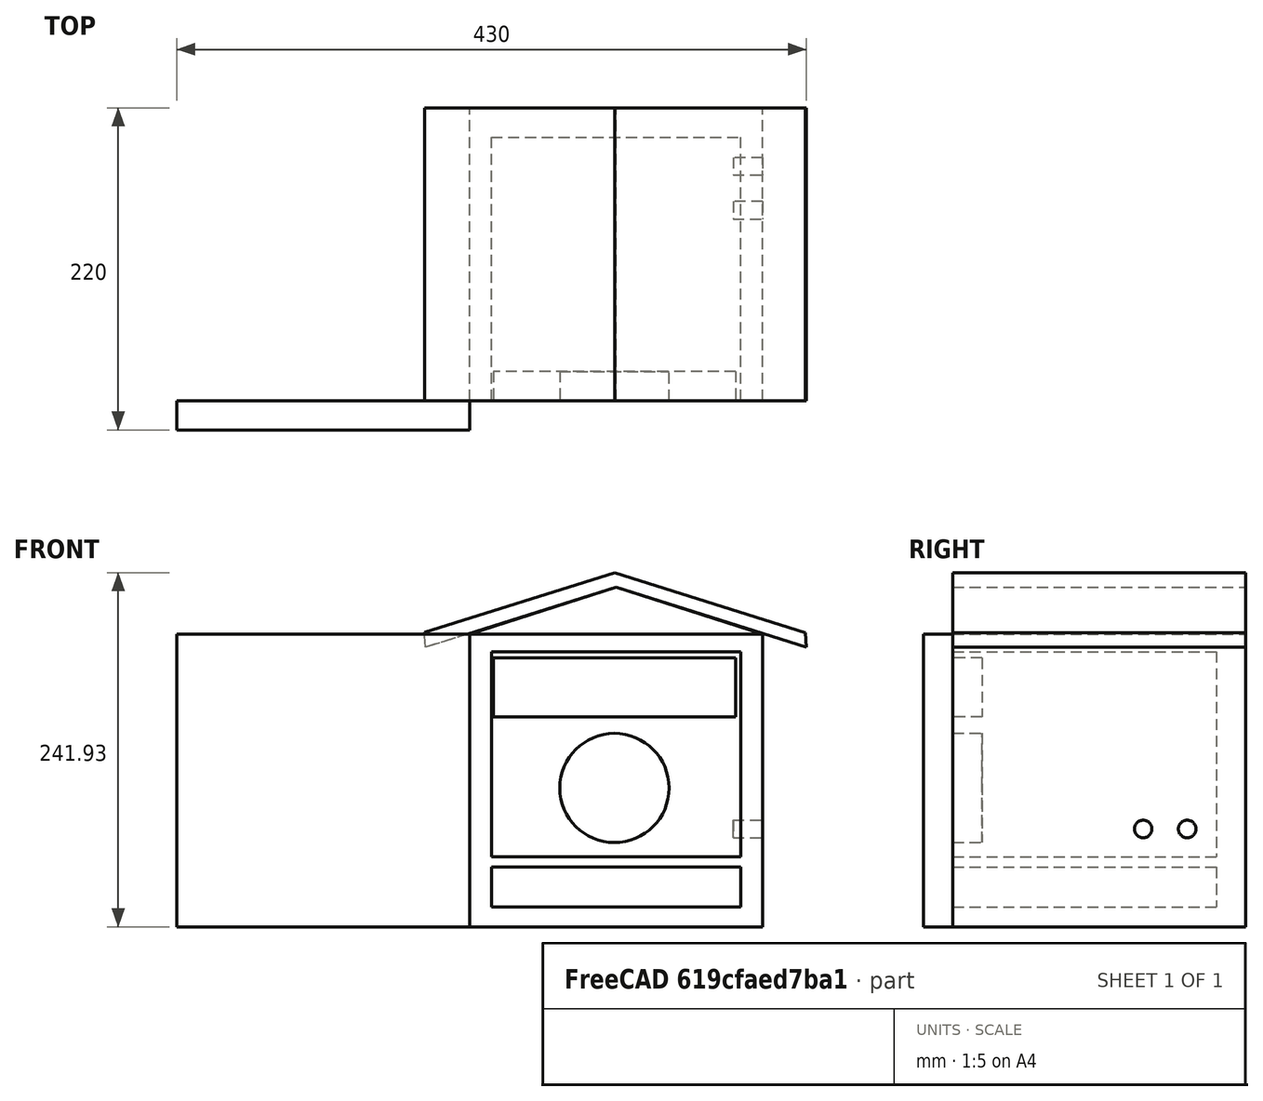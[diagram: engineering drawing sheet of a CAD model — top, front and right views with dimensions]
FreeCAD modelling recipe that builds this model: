
FCSTD DOCUMENT  (FreeCAD 0.16R6712 (Git))
Label: DSLR_Enclosure02
License: All rights reserved
LicenseURL: http://en.wikipedia.org/wiki/All_rights_reserved
objects: Drawing::FeatureViewPython×15, Drawing::FeatureViewPart×6, Sketcher::SketchObject×4, PartDesign::Pocket×3, Part::Box×2, PartDesign::Pad×1, Drawing::FeaturePage×1
note: 14 computed .brp shape members not serialized (recipe doc carries the construction recipe); baked Part::Feature solids carry a one-line shape summary decoded from their .brp

FEATURE [Part::Box] Box  label="Cube"
  Height = 200
  Length = 200
  Width = 200
FEATURE [Sketcher::SketchObject] Sketch
  Placement = pos=(0,0,0) rot=(1,0,0;1.5708rad)
  Support = -> Box [Face3]
  sketch-geometry (8):
    g0: LineSegment StartX=14.8295 StartY=187.945 StartZ=0 EndX=185.145 EndY=187.945 EndZ=0
    g1: LineSegment StartX=185.145 StartY=187.945 StartZ=0 EndX=185.145 EndY=47.8242 EndZ=0
    g2: LineSegment StartX=185.145 StartY=47.8242 StartZ=0 EndX=14.8295 EndY=47.8242 EndZ=0
    g3: LineSegment StartX=14.8295 StartY=47.8242 StartZ=0 EndX=14.8295 EndY=187.945 EndZ=0
    g4: LineSegment StartX=14.8558 StartY=40.8645 StartZ=0 EndX=185.13 EndY=40.8645 EndZ=0
    g5: LineSegment StartX=185.13 StartY=40.8645 StartZ=0 EndX=185.13 EndY=13.4597 EndZ=0
    g6: LineSegment StartX=185.13 StartY=13.4597 StartZ=0 EndX=14.8558 EndY=13.4597 EndZ=0
    g7: LineSegment StartX=14.8558 StartY=13.4597 StartZ=0 EndX=14.8558 EndY=40.8645 EndZ=0
  constraints (16):
    c: Coincident(g0,g1)
    c: Coincident(g1,g2)
    c: Coincident(g2,g3)
    c: Coincident(g3,g0)
    c: Horizontal(g0)
    c: Horizontal(g2)
    c: Vertical(g1)
    c: Vertical(g3)
    c: Coincident(g4,g5)
    c: Coincident(g5,g6)
    c: Coincident(g6,g7)
    c: Coincident(g7,g4)
    c: Horizontal(g4)
    c: Horizontal(g6)
    c: Vertical(g5)
    c: Vertical(g7)
FEATURE [Sketcher::SketchObject] Sketch002
  Placement = pos=(0,0,0) rot=(1,0,0;1.5708rad)
  sketch-geometry (9):
    g0: LineSegment StartX=100.011 StartY=231.935 StartZ=0 EndX=-30 EndY=191.024 EndZ=0
    g1: LineSegment StartX=-30 StartY=191.024 StartZ=0 EndX=-30.8025 EndY=201.024 EndZ=0
    g2: LineSegment StartX=-30.8025 StartY=201.024 StartZ=0 EndX=99.2083 EndY=241.935 EndZ=0
    g3: LineSegment StartX=99.2083 StartY=241.935 StartZ=0 EndX=229.197 EndY=200.955 EndZ=0
    g4: LineSegment StartX=229.197 StartY=200.955 StartZ=0 EndX=230 EndY=190.955 EndZ=0
    g5: LineSegment StartX=230 StartY=190.955 StartZ=0 EndX=100.011 EndY=231.935 EndZ=0
    g6: LineSegment StartX=100.011 StartY=231.935 StartZ=0 EndX=200.172 EndY=199.975 EndZ=0
    g7: LineSegment StartX=200.172 StartY=199.975 StartZ=0 EndX=0.002512 EndY=199.975 EndZ=0
    g8: LineSegment StartX=0.002512 StartY=199.975 StartZ=0 EndX=100.011 EndY=231.935 EndZ=0
  constraints (19):
    c: Coincident(g0,g1)
    c: Coincident(g1,g2)
    c: Coincident(g2,g3)
    c: Coincident(g3,g4)
    c: Coincident(g4,g5)
    c: Coincident(g5,g0)
    c: Equal(g2,g3)
    c: Equal(g0,g5)
    c: Equal(g4,g1)
    c: Parallel(g2,g0)
    c: Parallel(g3,g5)
    c: DistanceX(g0,g4) = 260
    c: DistanceY(g0,g1) = 10
    c: DistanceX(g0,g-1) = 30
    c: Coincident(g0,g6)
    c: Coincident(g6,g7)
    c: Horizontal(g7)
    c: Coincident(g7,g8)
    c: Coincident(g8,g6)
FEATURE [PartDesign::Pad] Pad
  Length = 200
  Length2 = 100
  Placement = pos=(0,0,0) rot=(1,0,0;1.5708rad)
  Reversed = true
  Sketch = -> Sketch002
  Type = 0
FEATURE [Part::Box] Box001  label="Cube001"
  Height = 200
  Length = 200
  Placement = pos=(0,0,0) rot=(0,0,1;3.14159rad)
  Width = 20
FEATURE [Sketcher::SketchObject] Sketch004
  Placement = pos=(0,-20,0) rot=(1,0,0;1.5708rad)
  Support = -> Box001 [Face4]
  sketch-geometry (5):
    g0: LineSegment StartX=-181.686 StartY=183.611 StartZ=0 EndX=-16.1366 EndY=183.611 EndZ=0
    g1: LineSegment StartX=-16.1366 StartY=183.611 StartZ=0 EndX=-16.1366 EndY=143.38 EndZ=0
    g2: LineSegment StartX=-16.1366 StartY=143.38 StartZ=0 EndX=-181.686 EndY=143.38 EndZ=0
    g3: LineSegment StartX=-181.686 StartY=143.38 StartZ=0 EndX=-181.686 EndY=183.611 EndZ=0
    g4: Circle CenterX=-98.9114 CenterY=94.8249 CenterZ=0 NormalX=0 NormalY=0 NormalZ=1 Radius=37.2966
  constraints (8):
    c: Coincident(g0,g1)
    c: Coincident(g1,g2)
    c: Coincident(g2,g3)
    c: Coincident(g3,g0)
    c: Horizontal(g0)
    c: Horizontal(g2)
    c: Vertical(g1)
    c: Vertical(g3)
FEATURE [PartDesign::Pocket] Pocket003
  Length = 20
  Placement = pos=(0,0,0) rot=(0,0,1;3.14159rad)
  Sketch = -> Sketch004
  Type = 0
FEATURE [Drawing::FeatureViewPart] Ortho  label="RightSide"
  Direction = (1,0,0)
  HiddenWidth = 0.15
  LineWidth = 0.35
  Rotation = -90
  Scale = 0.25
  ShowHiddenLines = false
  ShowSmoothLines = false
  Tolerance = 0.05
  ViewResult = <g id="RightSide"\n   transform="rotate(-90,165,150) translate(165,150) scale(0.25,0.25)"\n  >\n<g   stroke="rgb(0, 0, 0)"\n   stroke-width="1.4"\n   stroke-linecap="butt"\n   stroke-linejoin="miter"\n   fill="none"\n   transform="scale(1,-1)"\n  >\n<path id= "1" d=" M 0 0 L 199.975 0 " />\n<path id= "2" d=" M 0 -200 L 190.955 -200 " />\n<path id= "3" d=" M 0 0 L 0 -200 " />\n<circle cx ="66.8362" cy ="-160.008" r ="6" /><circle cx ="66.8362" cy ="-130.008" r ="6" /><path id= "6" d=" M 231.935 -1.545e-013 L 199.975 -1.3321e-013 " />\n<path id= "7" d=" M 190.955 -1.27202e-013 L 190.955 -200 " />\n<path id= "8" d=" M 200.955 -1.33863e-013 L 200.955 -200 " />\n<path id= "9" d=" M 200.955 -1.33863e-013 L 190.955 -1.27202e-013 " />\n<path id= "10" d=" M 200.955 -200 L 190.955 -200 " />\n<path id= "11" d=" M 231.935 -1.545e-013 L 199.975 -1.3321e-013 " />\n<path id= "12" d=" M 241.935 -1.61161e-013 L 200.955 -1.33863e-013 " />\n<path id= "13" d=" M 241.935 -200 L 200.955 -200 " />\n<path id= "14" d=" M 241.935 -1.61161e-013 L 241.935 -200 " />\n</g>\n</g>
  Visible = true
  X = 165
  Y = 150
FEATURE [Drawing::FeatureViewPart] Ortho001  label="TopView"
  Direction = (0,0,1)
  HiddenWidth = 0.15
  LineWidth = 0.35
  Rotation = 90
  Scale = 0.25
  ShowHiddenLines = false
  ShowSmoothLines = false
  Tolerance = 0.05
  ViewResult = <g id="TopView"\n   transform="rotate(90,30,110) translate(30,110) scale(0.25,0.25)"\n  >\n<g   stroke="rgb(0, 0, 0)"\n   stroke-width="1.4"\n   stroke-linecap="butt"\n   stroke-linejoin="miter"\n   fill="none"\n   transform="scale(1,-1)"\n  >\n<path id= "1" d=" M 0 0 L 0.0817739 0 " />\n<path id= "2" d=" M 185.274 1.04694e-014 L 14.4488 1.04694e-014 " />\n<path id= "3" d=" M 184.724 3.01073e-015 L 14.7262 3.01073e-015 " />\n<path id= "4" d=" M 0.0817739 1.33227e-013 L 100.011 1.545e-013 " />\n<path id= "5" d=" M 0.0817739 200 L 99.2083 200 " />\n<path id= "6" d=" M 100.011 1.545e-013 L 200.172 1.3321e-013 " />\n<path id= "7" d=" M 230 1.27202e-013 L 230 200 " />\n<path id= "8" d=" M 229.197 1.33863e-013 L 229.197 200 " />\n<path id= "9" d=" M 229.197 1.33863e-013 L 230 1.27202e-013 " />\n<path id= "10" d=" M 229.197 200 L 230 200 " />\n<path id= "11" d=" M -30.8025 1.33909e-013 L 99.2083 1.61161e-013 " />\n<path id= "12" d=" M 99.2083 1.61161e-013 L 229.197 1.33863e-013 " />\n<path id= "13" d=" M -30.8025 200 L 99.2083 200 " />\n<path id= "14" d=" M 99.2083 200 L 229.197 200 " />\n<path id= "15" d=" M 99.2083 1.61161e-013 L 99.2083 200 " />\n<path id= "16" d=" M -30.8025 1.33909e-013 L -30.8025 200 " />\n</g>\n</g>
  Visible = true
  X = 30
  Y = 110
FEATURE [Drawing::FeatureViewPart] Ortho002  label="BackView"
  Direction = (0,1,0)
  HiddenWidth = 0.15
  LineWidth = 0.35
  Rotation = -90
  Scale = 0.25
  ShowHiddenLines = false
  ShowSmoothLines = false
  Tolerance = 0.05
  ViewResult = <g id="BackView"\n   transform="rotate(-90,150,150) translate(150,150) scale(0.25,0.25)"\n  >\n<g   stroke="rgb(0, 0, 0)"\n   stroke-width="1.4"\n   stroke-linecap="butt"\n   stroke-linejoin="miter"\n   fill="none"\n   transform="scale(1,-1)"\n  >\n<path id= "1" d=" M 0 0 L 200 0 " />\n<path id= "2" d=" M 200 0 L 200 0.0817739 " />\n<path id= "3" d=" M 0 200 L 199.975 200 " />\n<path id= "4" d=" M 199.975 200 L 199.975 0.002512 " />\n<path id= "5" d=" M 199.975 0.002512 L 200 0.0817739 " />\n<path id= "6" d=" M 0 0 L 0 200 " />\n<path id= "7" d=" M 200 0.0817739 L 231.935 100.011 " />\n<path id= "8" d=" M 199.975 200 L 200 200 " />\n<path id= "9" d=" M 200 0.0817739 L 200 200 " />\n<path id= "10" d=" M 199.975 200.172 L 199.975 200 " />\n<path id= "11" d=" M 231.935 100.011 L 199.975 200.172 " />\n<path id= "12" d=" M 190.955 230 L 231.935 100.011 " />\n<path id= "13" d=" M 200.955 229.197 L 190.955 230 " />\n<path id= "14" d=" M 231.935 100.011 L 191.024 -30 " />\n<path id= "15" d=" M 191.024 -30 L 201.024 -30.8025 " />\n<path id= "16" d=" M 201.024 -30.8025 L 241.935 99.2083 " />\n<path id= "17" d=" M 241.935 99.2083 L 200.955 229.197 " />\n</g>\n</g>
  Visible = true
  X = 150
  Y = 150
FEATURE [Drawing::FeatureViewPart] Ortho003  label="FrontView"
  Direction = (0,-1,0)
  HiddenWidth = 0.15
  LineWidth = 0.35
  Rotation = 90
  Scale = 0.25
  ShowHiddenLines = false
  ShowSmoothLines = false
  Tolerance = 0.05
  ViewResult = <blob: 2083 chars omitted>
  Visible = true
  X = 30
  Y = 80
FEATURE [Drawing::FeatureViewPart] Ortho006  label="3DView"
  Direction = (0.57735,-0.57735,0.57735)
  HiddenWidth = 0.15
  LineWidth = 0.35
  Rotation = 60
  Scale = 0.15
  ShowHiddenLines = false
  ShowSmoothLines = false
  Tolerance = 0.05
  ViewResult = <blob: 2977 chars omitted>
  Visible = true
  X = 240
  Y = 50
FEATURE [Drawing::FeatureViewPart] Ortho007  label="LeftSide"
  Direction = (-1,0,0)
  HiddenWidth = 0.15
  LineWidth = 0.35
  Rotation = 90
  Scale = 0.25
  ShowHiddenLines = false
  ShowSmoothLines = false
  Tolerance = 0.05
  ViewResult = <g id="LeftSide"\n   transform="rotate(90,280,150) translate(280,150) scale(0.25,0.25)"\n  >\n<g   stroke="rgb(0, 0, 0)"\n   stroke-width="1.4"\n   stroke-linecap="butt"\n   stroke-linejoin="miter"\n   fill="none"\n   transform="scale(1,-1)"\n  >\n<path id= "1" d=" M 0 0 L -200 0 " />\n<path id= "2" d=" M 0 -200 L -191.024 -200 " />\n<path id= "3" d=" M 0 0 L 0 -200 " />\n<path id= "4" d=" M -200 -1.33227e-013 L -231.935 -1.545e-013 " />\n<path id= "5" d=" M -201.024 -200 L -231.935 -200 " />\n<path id= "6" d=" M -200 -1.33227e-013 L -231.935 -1.545e-013 " />\n<path id= "7" d=" M -190.955 -200 L -191.024 -200 " />\n<path id= "8" d=" M -201.024 -200 L -231.935 -200 " />\n<path id= "9" d=" M -191.024 -1.27247e-013 L -191.024 -200 " />\n<path id= "10" d=" M -191.024 -1.27247e-013 L -201.024 -1.33909e-013 " />\n<path id= "11" d=" M -201.024 -1.33909e-013 L -241.935 -1.61161e-013 " />\n<path id= "12" d=" M -191.024 -200 L -201.024 -200 " />\n<path id= "13" d=" M -201.024 -200 L -241.935 -200 " />\n<path id= "14" d=" M -241.935 -1.61161e-013 L -241.935 -200 " />\n<path id= "15" d=" M -201.024 -1.33909e-013 L -201.024 -200 " />\n</g>\n</g>
  Visible = true
  X = 280
  Y = 150
FEATURE [Drawing::FeatureViewPython] dim001  # drawing view (typed FeaturePython)
  Rotation = 0
  ViewResult = <g> \n  <line x1="80.000000" y1="82.000000" x2="80.000000" y2="89.389127" style="stroke:rgb(0,0,255);stroke-width:0.50" />\n<line x1="30.000000" y1="82.000000" x2="30.000000" y2="89.389127" style="stroke:rgb(0,0,255);stroke-width:0.50" />\n<line x1="80.000000" y1="88.389127" x2="30.000000" y2="88.389127" style="stroke:rgb(0,0,255);stroke-width:0.50" /> \n  <polygon points="30.000000,88.389127 33.000000,89.389127 34.000000,88.389127 33.000000,87.389127" style="fill:rgb(0,0,255);stroke:rgb(0,0,255);stroke-width:0" /><polygon points="80.000000,88.389127 77.000000,87.389127 76.000000,88.389127 77.000000,89.389127" style="fill:rgb(0,0,255);stroke:rgb(0,0,255);stroke-width:0" /> \n  <text x="55.000000" y="86.389127" font-family="inherit" font-size="3.6" fill="rgb(0,0,255)" text-anchor="middle" transform="rotate(0.000000 55.000000,86.389127)" >200</text> </g>
  Visible = true
  X = 0
  Y = 0
  arrowL1 = 3
  arrowL2 = 1
  arrowW = 2
  arrow_scheme = 0
  autoPlaceOffset = 2
  autoPlaceText = true
  click1_x = 49.3118
  click1_y = 88.3891
  click2_x = 49.3118
  click2_y = 88.3891
  comma_decimal_place = false
  dimension_line_overshoot = 1
  gap_datum_points = 2
  halfDimension_linear = false
  lineColor = rgb(0,0,255)
  strokeWidth = 0.5
  textFormat_linear = %(value)3.3f
  textRenderer_color = rgb(0,0,255)
  textRenderer_family = inherit
  textRenderer_size = 3.6
  unit_custom_scale = 1
  unit_scheme = 0
FEATURE [Drawing::FeatureViewPython] dim004  # drawing view (typed FeaturePython)
  Rotation = 0
  ViewResult = <g> \n  <line x1="30.000000" y1="169.299250" x2="30.000000" y2="180.197324" style="stroke:rgb(0,0,255);stroke-width:0.50" />\n<line x1="80.000000" y1="169.299250" x2="80.000000" y2="180.197324" style="stroke:rgb(0,0,255);stroke-width:0.50" />\n<line x1="30.000000" y1="179.197324" x2="80.000000" y2="179.197324" style="stroke:rgb(0,0,255);stroke-width:0.50" /> \n  <polygon points="80.000000,179.197324 77.000000,178.197324 76.000000,179.197324 77.000000,180.197324" style="fill:rgb(0,0,255);stroke:rgb(0,0,255);stroke-width:0" /><polygon points="30.000000,179.197324 33.000000,180.197324 34.000000,179.197324 33.000000,178.197324" style="fill:rgb(0,0,255);stroke:rgb(0,0,255);stroke-width:0" /> \n  <text x="55.000000" y="177.197324" font-family="inherit" font-size="3.6" fill="rgb(0,0,255)" text-anchor="middle" transform="rotate(0.000000 55.000000,177.197324)" >200</text> </g>
  Visible = true
  X = 0
  Y = 0
  arrowL1 = 3
  arrowL2 = 1
  arrowW = 2
  arrow_scheme = 0
  autoPlaceOffset = 2
  autoPlaceText = true
  click1_x = 52.1961
  click1_y = 179.197
  click2_x = 52.1961
  click2_y = 179.197
  comma_decimal_place = false
  dimension_line_overshoot = 1
  gap_datum_points = 2
  halfDimension_linear = false
  lineColor = rgb(0,0,255)
  strokeWidth = 0.5
  textFormat_linear = %(value)3.3f
  textRenderer_color = rgb(0,0,255)
  textRenderer_family = inherit
  textRenderer_size = 3.6
  unit_custom_scale = 1
  unit_scheme = 0
FEATURE [Drawing::FeatureViewPython] dimStack001  # drawing view (typed FeaturePython)
  Rotation = 0
  ViewResult = <g> <line x1="78.181000" y1="76.610225" x2="97.530230" y2="76.610225" style="stroke:rgb(0,0,255);stroke-width:0.50" />\n<line x1="78.181000" y1="71.462275" x2="97.530230" y2="71.462275" style="stroke:rgb(0,0,255);stroke-width:0.50" />\n<line x1="96.530230" y1="76.610225" x2="96.530230" y2="71.462275" style="stroke:rgb(0,0,255);stroke-width:0.50" />\n<polygon points="96.530230,76.610225 95.530230,79.610225 96.530230,80.610225 97.530230,79.610225" style="fill:rgb(0,0,255);stroke:rgb(0,0,255);stroke-width:0" />\n<polygon points="96.530230,71.462275 97.530230,68.462275 96.530230,67.462275 95.530230,68.462275" style="fill:rgb(0,0,255);stroke:rgb(0,0,255);stroke-width:0" />\n<text x="94.530230" y="74.036250" font-family="inherit" font-size="3.6" fill="rgb(0,0,255)" text-anchor="middle" transform="rotate(-90.000000 94.530230,74.036250)" >20.592</text> </g> 
  Visible = true
  X = 0
  Y = 0
  arrowL1 = 3
  arrowL2 = 1
  arrowW = 2
  arrow_scheme = 0
  autoPlaceOffset = 2
  click1_x = 96.5302
  click1_y = 69.3932
  comma_decimal_place = false
  dimension_line_overshoot = 1
  gap_datum_points = 2
  lineColor = rgb(0,0,255)
  stack_offset = 7
  stack_offset0 = 0
  strokeWidth = 0.5
  textFormat_linear = %(value)3.3f
  textRenderer_color = rgb(0,0,255)
  textRenderer_family = inherit
  textRenderer_size = 3.6
  unit_custom_scale = 1
  unit_scheme = 0
FEATURE [Drawing::FeatureViewPython] dimStack002  # drawing view (typed FeaturePython)
  Rotation = 0
  ViewResult = <g> <line x1="78.318500" y1="32.943500" x2="97.530230" y2="32.943500" style="stroke:rgb(0,0,255);stroke-width:0.50" />\n<line x1="78.318500" y1="68.212450" x2="97.530230" y2="68.212450" style="stroke:rgb(0,0,255);stroke-width:0.50" />\n<line x1="96.530230" y1="32.943500" x2="96.530230" y2="68.212450" style="stroke:rgb(0,0,255);stroke-width:0.50" />\n<polygon points="96.530230,32.943500 95.530230,35.943500 96.530230,36.943500 97.530230,35.943500" style="fill:rgb(0,0,255);stroke:rgb(0,0,255);stroke-width:0" />\n<polygon points="96.530230,68.212450 97.530230,65.212450 96.530230,64.212450 95.530230,65.212450" style="fill:rgb(0,0,255);stroke:rgb(0,0,255);stroke-width:0" />\n<text x="94.530230" y="50.577975" font-family="inherit" font-size="3.6" fill="rgb(0,0,255)" text-anchor="middle" transform="rotate(-90.000000 94.530230,50.577975)" >141.076</text> </g> 
  Visible = true
  X = 0
  Y = 0
  arrowL1 = 3
  arrowL2 = 1
  arrowW = 2
  arrow_scheme = 0
  autoPlaceOffset = 2
  click1_x = 96.5302
  click1_y = 62.609
  comma_decimal_place = false
  dimension_line_overshoot = 1
  gap_datum_points = 2
  lineColor = rgb(0,0,255)
  stack_offset = 7
  stack_offset0 = 0
  strokeWidth = 0.5
  textFormat_linear = %(value)3.3f
  textRenderer_color = rgb(0,0,255)
  textRenderer_family = inherit
  textRenderer_size = 3.6
  unit_custom_scale = 1
  unit_scheme = 0
FEATURE [Drawing::FeatureViewPython] dim003  # drawing view (typed FeaturePython)
  Rotation = 0
  ViewResult = <g> \n  <line x1="31.612200" y1="68.212450" x2="16.251387" y2="68.212450" style="stroke:rgb(0,0,255);stroke-width:0.50" />\n<line x1="31.612200" y1="32.943500" x2="16.251387" y2="32.943500" style="stroke:rgb(0,0,255);stroke-width:0.50" />\n<line x1="17.251387" y1="68.212450" x2="17.251387" y2="32.943500" style="stroke:rgb(0,0,255);stroke-width:0.50" /> \n  <polygon points="17.251387,32.943500 16.251387,35.943500 17.251387,36.943500 18.251387,35.943500" style="fill:rgb(0,0,255);stroke:rgb(0,0,255);stroke-width:0" /><polygon points="17.251387,68.212450 18.251387,65.212450 17.251387,64.212450 16.251387,65.212450" style="fill:rgb(0,0,255);stroke:rgb(0,0,255);stroke-width:0" /> \n  <text x="15.251387" y="50.577975" font-family="inherit" font-size="3.6" fill="rgb(0,0,255)" text-anchor="middle" transform="rotate(-90.000000 15.251387,50.577975)" >141.076</text> </g>
  Visible = true
  X = 0
  Y = 0
  arrowL1 = 3
  arrowL2 = 1
  arrowW = 2
  arrow_scheme = 0
  autoPlaceOffset = 2
  autoPlaceText = true
  click1_x = 17.2514
  click1_y = 47.4898
  click2_x = 17.2514
  click2_y = 47.4898
  comma_decimal_place = false
  dimension_line_overshoot = 1
  gap_datum_points = 2
  halfDimension_linear = false
  lineColor = rgb(0,0,255)
  strokeWidth = 0.5
  textFormat_linear = %(value)3.3f
  textRenderer_color = rgb(0,0,255)
  textRenderer_family = inherit
  textRenderer_size = 3.6
  unit_custom_scale = 1
  unit_scheme = 0
FEATURE [Drawing::FeatureViewPython] dim005  # drawing view (typed FeaturePython)
  Rotation = 0
  ViewResult = <g> \n  <line x1="87.500000" y1="30.261250" x2="87.500000" y2="12.956178" style="stroke:rgb(0,0,255);stroke-width:0.50" />\n<line x1="55.002750" y1="20.016250" x2="55.002750" y2="12.956178" style="stroke:rgb(0,0,255);stroke-width:0.50" />\n<line x1="87.500000" y1="13.956178" x2="55.002750" y2="13.956178" style="stroke:rgb(0,0,255);stroke-width:0.50" /> \n  <polygon points="55.002750,13.956178 58.002750,14.956178 59.002750,13.956178 58.002750,12.956178" style="fill:rgb(0,0,255);stroke:rgb(0,0,255);stroke-width:0" /><polygon points="87.500000,13.956178 84.500000,12.956178 83.500000,13.956178 84.500000,14.956178" style="fill:rgb(0,0,255);stroke:rgb(0,0,255);stroke-width:0" /> \n  <text x="71.251375" y="11.956178" font-family="inherit" font-size="3.6" fill="rgb(0,0,255)" text-anchor="middle" transform="rotate(0.000000 71.251375,11.956178)" >129.989</text> </g>
  Visible = true
  X = 0
  Y = 0
  arrowL1 = 3
  arrowL2 = 1
  arrowW = 2
  arrow_scheme = 0
  autoPlaceOffset = 2
  autoPlaceText = true
  click1_x = 75.0145
  click1_y = 13.9562
  click2_x = 75.0145
  click2_y = 13.9562
  comma_decimal_place = false
  dimension_line_overshoot = 1
  gap_datum_points = 2
  halfDimension_linear = false
  lineColor = rgb(0,0,255)
  strokeWidth = 0.5
  textFormat_linear = %(value)3.3f
  textRenderer_color = rgb(0,0,255)
  textRenderer_family = inherit
  textRenderer_size = 3.6
  unit_custom_scale = 1
  unit_scheme = 0
FEATURE [Drawing::FeatureViewPython] dim006  # drawing view (typed FeaturePython)
  Rotation = 0
  ViewResult = <g> \n  <line x1="54.802075" y1="17.516250" x2="54.802075" y2="18.189745" style="stroke:rgb(0,0,255);stroke-width:0.50" />\n<line x1="87.299250" y1="27.761250" x2="87.299250" y2="18.189745" style="stroke:rgb(0,0,255);stroke-width:0.50" />\n<line x1="54.802075" y1="19.189745" x2="87.299250" y2="19.189745" style="stroke:rgb(0,0,255);stroke-width:0.50" /> \n  <polygon points="87.299250,19.189745 84.299250,18.189745 83.299250,19.189745 84.299250,20.189745" style="fill:rgb(0,0,255);stroke:rgb(0,0,255);stroke-width:0" /><polygon points="54.802075,19.189745 57.802075,20.189745 58.802075,19.189745 57.802075,18.189745" style="fill:rgb(0,0,255);stroke:rgb(0,0,255);stroke-width:0" /> \n  <text x="71.050663" y="17.189745" font-family="inherit" font-size="3.6" fill="rgb(0,0,255)" text-anchor="middle" transform="rotate(0.000000 71.050663,17.189745)" >129.989</text> </g>
  Visible = true
  X = 0
  Y = 0
  arrowL1 = 3
  arrowL2 = 1
  arrowW = 2
  arrow_scheme = 0
  autoPlaceOffset = 2
  autoPlaceText = true
  click1_x = 73.0761
  click1_y = 19.1897
  click2_x = 73.0761
  click2_y = 19.1897
  comma_decimal_place = false
  dimension_line_overshoot = 1
  gap_datum_points = 2
  halfDimension_linear = false
  lineColor = rgb(0,0,255)
  strokeWidth = 0.5
  textFormat_linear = %(value)3.3f
  textRenderer_color = rgb(0,0,255)
  textRenderer_family = inherit
  textRenderer_size = 3.6
  unit_custom_scale = 1
  unit_scheme = 0
FEATURE [Drawing::FeatureViewPython] dia002  # drawing view (typed FeaturePython)
  Rotation = 0
  ViewResult = <g>  <circle cx ="205.002000" cy ="133.290950" r="0.250000" stroke="none" fill="rgb(0,0,255)" /> \n<line x1="190.054261" y1="147.558292" x2="206.087068" y2="132.255273" style="stroke:rgb(0,0,255);stroke-width:0.50" />\n<polygon points="203.916932,134.326627 201.056345,135.674603 201.023418,137.088434 202.437248,137.121361" style="fill:rgb(0,0,255);stroke:rgb(0,0,255);stroke-width:0" />\n<polygon points="206.087068,132.255273 208.947655,130.907297 208.980582,129.493466 207.566752,129.460539" style="fill:rgb(0,0,255);stroke:rgb(0,0,255);stroke-width:0" />\n<line x1="190.054261" y1="147.558292" x2="180.019068" y2="147.558292" style="stroke:rgb(0,0,255);stroke-width:0.50" />\n<text x="185.036664" y="145.558292" font-family="inherit" font-size="3.6" fill="rgb(0,0,255)" text-anchor="middle" transform="rotate(0.000000 185.036664,145.558292)" >Ø12</text> </g>
  Visible = true
  X = 0
  Y = 0
  arrowL1 = 3
  arrowL2 = 1
  arrowW = 2
  arrow_scheme = 0
  autoPlaceOffset = 2
  autoPlaceText = true
  centerPointDia = 0.5
  click1_x = 190.054
  click1_y = 147.558
  click2_x = 180.019
  click2_y = 146.534
  click3_x = 180.019
  click3_y = 146.534
  comma_decimal_place = false
  lineColor = rgb(0,0,255)
  strokeWidth = 0.5
  textFormat_circular = Ø%(value)3.3f
  textRenderer_color = rgb(0,0,255)
  textRenderer_family = inherit
  textRenderer_size = 3.6
  unit_custom_scale = 1
  unit_scheme = 0
FEATURE [Drawing::FeatureViewPython] dim010  # drawing view (typed FeaturePython)
  Rotation = 0
  ViewResult = <g> \n  <line x1="217.000000" y1="89.516250" x2="224.462916" y2="89.516250" style="stroke:rgb(0,0,255);stroke-width:0.50" />\n<line x1="217.000000" y1="99.761250" x2="224.462916" y2="99.761250" style="stroke:rgb(0,0,255);stroke-width:0.50" />\n<line x1="223.462916" y1="89.516250" x2="223.462916" y2="99.761250" style="stroke:rgb(0,0,255);stroke-width:0.50" /> \n  <polygon points="223.462916,99.761250 224.462916,96.761250 223.462916,95.761250 222.462916,96.761250" style="fill:rgb(0,0,255);stroke:rgb(0,0,255);stroke-width:0" /><polygon points="223.462916,89.516250 222.462916,92.516250 223.462916,93.516250 224.462916,92.516250" style="fill:rgb(0,0,255);stroke:rgb(0,0,255);stroke-width:0" /> \n  <text x="221.462916" y="94.638750" font-family="inherit" font-size="3.6" fill="rgb(0,0,255)" text-anchor="middle" transform="rotate(-90.000000 221.462916,94.638750)" >40.98</text> </g>
  Visible = true
  X = 0
  Y = 0
  arrowL1 = 3
  arrowL2 = 1
  arrowW = 2
  arrow_scheme = 0
  autoPlaceOffset = 2
  autoPlaceText = true
  click1_x = 223.463
  click1_y = 97.8447
  click2_x = 223.463
  click2_y = 97.8447
  comma_decimal_place = false
  dimension_line_overshoot = 1
  gap_datum_points = 2
  halfDimension_linear = false
  lineColor = rgb(0,0,255)
  strokeWidth = 0.5
  textFormat_linear = %(value)3.3f
  textRenderer_color = rgb(0,0,255)
  textRenderer_family = inherit
  textRenderer_size = 3.6
  unit_custom_scale = 1
  unit_scheme = 0
FEATURE [Drawing::FeatureViewPython] dim008  # drawing view (typed FeaturePython)
  Rotation = 0
  ViewResult = <g> \n  <line x1="217.000000" y1="99.761250" x2="224.288725" y2="99.761250" style="stroke:rgb(0,0,255);stroke-width:0.50" />\n<line x1="217.000000" y1="102.261250" x2="224.288725" y2="102.261250" style="stroke:rgb(0,0,255);stroke-width:0.50" />\n<line x1="223.288725" y1="99.761250" x2="223.288725" y2="102.261250" style="stroke:rgb(0,0,255);stroke-width:0.50" /> \n  <polygon points="223.288725,102.261250 222.288725,105.261250 223.288725,106.261250 224.288725,105.261250" style="fill:rgb(0,0,255);stroke:rgb(0,0,255);stroke-width:0" /><polygon points="223.288725,99.761250 224.288725,96.761250 223.288725,95.761250 222.288725,96.761250" style="fill:rgb(0,0,255);stroke:rgb(0,0,255);stroke-width:0" /> \n  <text x="221.288725" y="101.011250" font-family="inherit" font-size="3.6" fill="rgb(0,0,255)" text-anchor="middle" transform="rotate(-90.000000 221.288725,101.011250)" >10</text> </g>
  Visible = true
  X = 0
  Y = 0
  arrowL1 = 3
  arrowL2 = 1
  arrowW = 2
  arrow_scheme = 0
  autoPlaceOffset = 2
  autoPlaceText = true
  click1_x = 223.289
  click1_y = 100.978
  click2_x = 223.289
  click2_y = 100.978
  comma_decimal_place = false
  dimension_line_overshoot = 1
  gap_datum_points = 2
  halfDimension_linear = false
  lineColor = rgb(0,0,255)
  strokeWidth = 0.5
  textFormat_linear = %(value)3.3f
  textRenderer_color = rgb(0,0,255)
  textRenderer_family = inherit
  textRenderer_size = 3.6
  unit_custom_scale = 1
  unit_scheme = 0
FEATURE [Drawing::FeatureViewPython] dim007  # drawing view (typed FeaturePython)
  Rotation = 0
  ViewResult = <g> \n  <line x1="89.292833" y1="29.601165" x2="106.263266" y2="28.238440" style="stroke:rgb(0,0,255);stroke-width:0.50" />\n<line x1="89.493583" y1="32.101165" x2="106.464016" y2="30.738440" style="stroke:rgb(0,0,255);stroke-width:0.50" />\n<line x1="105.266474" y1="28.318482" x2="105.467224" y2="30.818482" style="stroke:rgb(0,0,255);stroke-width:0.50" /> \n  <polygon points="105.467224,30.818482 104.710560,33.888899 105.787394,34.805648 106.704143,33.728814" style="fill:rgb(0,0,255);stroke:rgb(0,0,255);stroke-width:0" /><polygon points="105.266474,28.318482 106.023138,25.248065 104.946305,24.331316 104.029556,25.408150" style="fill:rgb(0,0,255);stroke:rgb(0,0,255);stroke-width:0" /> \n  <text x="105.206764" y="27.574899" font-family="inherit" font-size="3.6" fill="rgb(0,0,255)" text-anchor="middle" transform="rotate(-4.591000 105.206764,27.574899)" >10.032</text> </g>
  Visible = true
  X = 0
  Y = 0
  arrowL1 = 3
  arrowL2 = 1
  arrowW = 2
  arrow_scheme = 0
  autoPlaceOffset = 2
  autoPlaceText = true
  click1_x = 105
  click1_y = 25
  click2_x = 105
  click2_y = 25
  comma_decimal_place = false
  dimension_line_overshoot = 1
  gap_datum_points = 2
  halfDimension_linear = false
  lineColor = rgb(0,0,255)
  strokeWidth = 0.5
  textFormat_linear = %(value)3.3f
  textRenderer_color = rgb(0,0,255)
  textRenderer_family = inherit
  textRenderer_size = 3.6
  unit_custom_scale = 1
  unit_scheme = 0
FEATURE [Drawing::FeatureViewPython] centerLines001  # drawing view (typed FeaturePython)
  Rotation = 0
  ViewResult = <g transform="scale(0.250000,0.250000)" stroke="rgb(0,0,255)"  stroke-width="1.280000" > <path d="M 790.008000,533.163800 L 790.008000,521.163800 "/>\n<path d="M 790.008000,533.163800 L 778.008000,533.163800 M 770.008000,533.163800 L 760.000000,533.163800 "/>\n<path d="M 790.008000,533.163800 L 790.008000,540.000000 "/>\n<path d="M 790.008000,533.163800 L 800.000000,533.163800 "/> </g> 
  Visible = true
  X = 0
  Y = 0
  centerLine_color = rgb(0,0,255)
  centerLine_len_dash = 6
  centerLine_len_dot = 3
  centerLine_len_gap = 2
  centerLine_width = 0.32
  click1_x = 190
  click1_y = 130
  click2_x = 200
  click2_y = 135
FEATURE [Drawing::FeatureViewPython] centerLines002  # drawing view (typed FeaturePython)
  Rotation = 0
  ViewResult = <g transform="scale(0.250000,0.250000)" stroke="rgb(0,0,255)"  stroke-width="1.280000" > <path d="M 820.008000,533.163800 L 820.008000,521.163800 "/>\n<path d="M 820.008000,533.163800 L 808.008000,533.163800 M 800.008000,533.163800 L 800.000000,533.163800 "/>\n<path d="M 820.008000,533.163800 L 820.008000,540.000000 "/>\n<path d="M 820.008000,533.163800 L 820.000000,533.163800 "/> </g> 
  Visible = true
  X = 0
  Y = 0
  centerLine_color = rgb(0,0,255)
  centerLine_len_dash = 6
  centerLine_len_dot = 3
  centerLine_len_gap = 2
  centerLine_width = 0.32
  click1_x = 200
  click1_y = 130
  click2_x = 205
  click2_y = 135
FEATURE [Drawing::FeatureViewPython] dim002  # drawing view (typed FeaturePython)
  Rotation = 0
  ViewResult = <g> \n  <line x1="197.502000" y1="128.290950" x2="197.502000" y2="119.000000" style="stroke:rgb(0,0,255);stroke-width:0.50" />\n<line x1="205.002000" y1="128.290950" x2="205.002000" y2="119.000000" style="stroke:rgb(0,0,255);stroke-width:0.50" />\n<line x1="197.502000" y1="120.000000" x2="205.002000" y2="120.000000" style="stroke:rgb(0,0,255);stroke-width:0.50" /> \n  <polygon points="205.002000,120.000000 208.002000,121.000000 209.002000,120.000000 208.002000,119.000000" style="fill:rgb(0,0,255);stroke:rgb(0,0,255);stroke-width:0" /><polygon points="197.502000,120.000000 194.502000,119.000000 193.502000,120.000000 194.502000,121.000000" style="fill:rgb(0,0,255);stroke:rgb(0,0,255);stroke-width:0" /> \n  <text x="201.252000" y="118.000000" font-family="inherit" font-size="3.6" fill="rgb(0,0,255)" text-anchor="middle" transform="rotate(0.000000 201.252000,118.000000)" >30</text> </g>
  Visible = true
  X = 0
  Y = 0
  arrowL1 = 3
  arrowL2 = 1
  arrowW = 2
  arrow_scheme = 0
  autoPlaceOffset = 2
  autoPlaceText = true
  click1_x = 200
  click1_y = 120
  click2_x = 200
  click2_y = 120
  comma_decimal_place = false
  dimension_line_overshoot = 1
  gap_datum_points = 2
  halfDimension_linear = false
  lineColor = rgb(0,0,255)
  strokeWidth = 0.5
  textFormat_linear = %(value)3.3f
  textRenderer_color = rgb(0,0,255)
  textRenderer_family = inherit
  textRenderer_size = 3.6
  unit_custom_scale = 1
  unit_scheme = 0
FEATURE [Drawing::FeatureViewPython] dia001  # drawing view (typed FeaturePython)
  Rotation = 0
  ViewResult = <g>  <circle cx ="197.502000" cy ="133.290950" r="0.250000" stroke="none" fill="rgb(0,0,255)" /> \n<line x1="188.638432" y1="142.273386" x2="198.555572" y2="132.223249" style="stroke:rgb(0,0,255);stroke-width:0.50" />\n<polygon points="196.448428,134.358651 193.629483,135.791672 193.638903,137.205855 195.053085,137.196435" style="fill:rgb(0,0,255);stroke:rgb(0,0,255);stroke-width:0" />\n<polygon points="198.555572,132.223249 201.374517,130.790228 201.365097,129.376045 199.950915,129.385465" style="fill:rgb(0,0,255);stroke:rgb(0,0,255);stroke-width:0" />\n<line x1="188.638432" y1="142.273386" x2="180.412375" y2="142.273386" style="stroke:rgb(0,0,255);stroke-width:0.50" />\n<text x="184.525403" y="140.273386" font-family="inherit" font-size="3.6" fill="rgb(0,0,255)" text-anchor="middle" transform="rotate(0.000000 184.525403,140.273386)" >Ø12</text> </g>
  Visible = true
  X = 0
  Y = 0
  arrowL1 = 3
  arrowL2 = 1
  arrowW = 2
  arrow_scheme = 0
  autoPlaceOffset = 2
  autoPlaceText = true
  centerPointDia = 0.5
  click1_x = 188.638
  click1_y = 142.273
  click2_x = 180.412
  click2_y = 139.656
  click3_x = 180.412
  click3_y = 139.656
  comma_decimal_place = false
  lineColor = rgb(0,0,255)
  strokeWidth = 0.5
  textFormat_circular = Ø%(value)3.3f
  textRenderer_color = rgb(0,0,255)
  textRenderer_family = inherit
  textRenderer_size = 3.6
  unit_custom_scale = 1
  unit_scheme = 0
FEATURE [Drawing::FeaturePage] Page
  EditableTexts = Designed by Name | Date | Scale | Weight | Title | Subtitle | Drawing number | Sheet
  Group = -> [Ortho,Ortho001,Ortho002,Ortho003,Ortho006,Ortho007,dim001,dim004,dimStack001,dimStack002,dim003,dim005,dim006,dia001,dia002,dim010,dim008,dim007,centerLines001,centerLines002,dim002]
FEATURE [PartDesign::Pocket] Pocket
  Length = 180
  Sketch = -> Sketch
  Type = 0
FEATURE [Sketcher::SketchObject] Sketch001
  Placement = pos=(200,0,0) rot=(0.57735,0.57735,0.57735;2.0944rad)
  Support = -> Pocket [Face6]
  sketch-geometry (2):
    g0: Circle CenterX=130.008 CenterY=66.8362 CenterZ=0 NormalX=0 NormalY=0 NormalZ=1 Radius=6
    g1: Circle CenterX=160.008 CenterY=66.8362 CenterZ=0 NormalX=0 NormalY=0 NormalZ=1 Radius=6
  constraints (4):
    c: Radius(g0) = 6
    c: Radius(g1) = 6
    c: DistanceY(g1,g0) = 0
    c: DistanceX(g0,g1) = 30
FEATURE [PartDesign::Pocket] Pocket004
  Length = 20
  Sketch = -> Sketch001
  Type = 0
